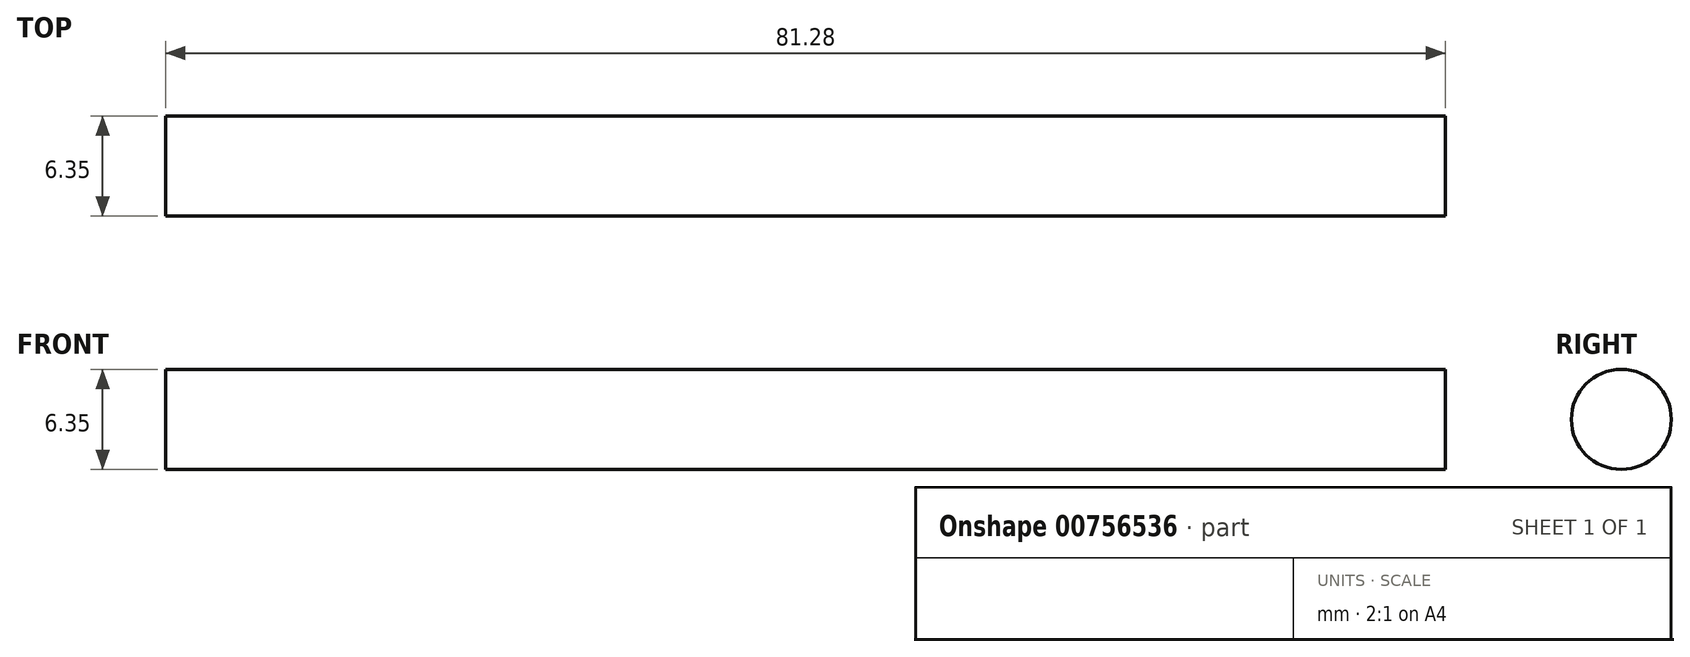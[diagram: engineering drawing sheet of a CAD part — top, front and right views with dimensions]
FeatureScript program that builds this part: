
annotation { "Feature Type Name" : "Feature", "Feature Type Description" : "" }
export const myFeature = defineFeature(function(context is Context, id is Id, definition is map)
    precondition{}
    {
        {
            var Q0;
            Q0=qCreatedBy(makeId("Right.planeOp"),FACE);
            var sketch = newSketch(context, id + "F0", { "sketchPlane" : qUnion([Q0])});
            skCircle(sketch, "E0", {"center": v(-3.09, 3.94) * mm, "radius": 3.18 * mm});
            skSolve(sketch);
        }
        {
            var Q0;
            Q0 = qSketchRegion(id + "F0", true);
            extrude(context, id + "F1", {"entities" : qUnion([Q0]), "depth" : 81.28 * mm, "offsetDistance" : 25.4 * mm});
        }
    });
